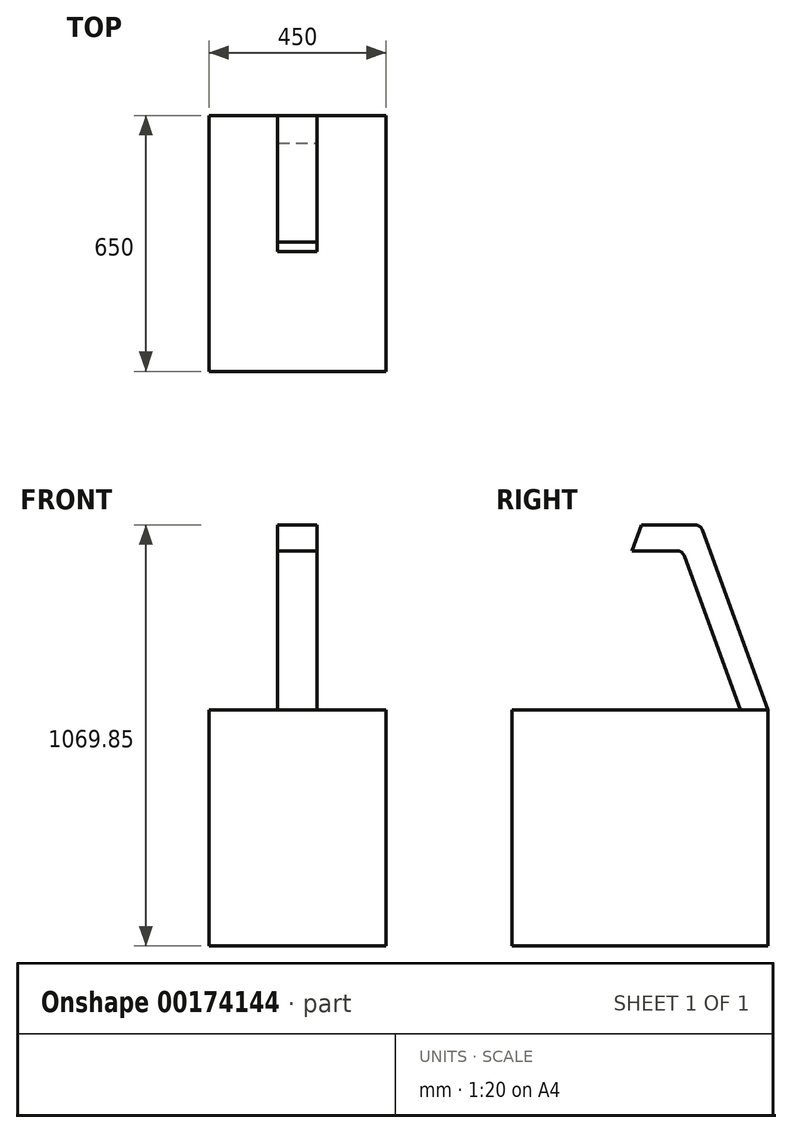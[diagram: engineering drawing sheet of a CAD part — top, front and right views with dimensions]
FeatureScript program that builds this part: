
annotation { "Feature Type Name" : "Feature", "Feature Type Description" : "" }
export const myFeature = defineFeature(function(context is Context, id is Id, definition is map)
    precondition{}
    {
        {
            var Q0;
            Q0=qCreatedBy(makeId("Top.planeOp"),FACE);
            var sketch = newSketch(context, id + "F0", { "sketchPlane" : qUnion([Q0])});
            skLineSegment(sketch, "E0.bottom", {"start": v(0, 0) * mm, "end": v(450, 0) * mm});
            skLineSegment(sketch, "E0.top", {"start": v(0, 650) * mm, "end": v(450, 650) * mm});
            skLineSegment(sketch, "E0.left", {"start": v(0, 0) * mm, "end": v(0, 650) * mm});
            skLineSegment(sketch, "E0.right", {"start": v(450, 0) * mm, "end": v(450, 650) * mm});
            skSolve(sketch);
        }
        {
            var Q0;
            Q0=makeQuery(id+"F0.imprint","IMPRINT",FACE,{"disambiguationData":[TD([[makeQuery(id+"F0.imprint","IMPRINT",EDGE,{"derivedFrom":sQuery(id+"F0.wireOp",EDGE,"E0.bottom")}),1.0]])]});
            extrude(context, id + "F1", {"entities" : qUnion([Q0]), "depth" : 600 * mm});
        }
        {
            var Q0;
            Q0=makeQuery(id+"F1.opExtrude","CAP_FACE",FACE,{"disambiguationData":[OSD([sQuery(id+"F0.wireOp",EDGE,"E0.bottom"),sQuery(id+"F0.wireOp",EDGE,"E0.top"),sQuery(id+"F0.wireOp",EDGE,"E0.left"),sQuery(id+"F0.wireOp",EDGE,"E0.right")])],"isStart":false});
            var sketch = newSketch(context, id + "F2", { "sketchPlane" : qUnion([Q0])});
            skLineSegment(sketch, "E1.bottom", {"start": v(175, 650) * mm, "end": v(275, 650) * mm});
            skLineSegment(sketch, "E1.top", {"start": v(175, 580) * mm, "end": v(275, 580) * mm});
            skLineSegment(sketch, "E1.left", {"start": v(175, 650) * mm, "end": v(175, 580) * mm});
            skLineSegment(sketch, "E1.right", {"start": v(275, 650) * mm, "end": v(275, 580) * mm});
            skSolve(sketch);
        }
        {
            var Q0;
            Q0=qCreatedBy(makeId("Right.planeOp"),FACE);
            var Q1;
            Q1=makeQuery(id+"F1.opExtrude","SWEPT_FACE",FACE,{"disambiguationData":[OSD([sQuery(id+"F0.wireOp",EDGE,"E0.right")])]});
            cPlane(context, id + "F3", {"entities" : qUnion([Q0, Q1]), "cplaneType" : CPlaneType.MID_PLANE, "offset" : 25 * mm, "width" : 150 * mm, "height" : 150 * mm});
        }
        {
            var Q0;
            Q0=qCreatedBy(id+"F3.planeOp",FACE);
            var sketch = newSketch(context, id + "F4", { "sketchPlane" : qUnion([Q0])});
            skLineSegment(sketch, "E2", {"start": v(650, 600) * mm, "end": v(478.99, 1069.85) * mm});
            skLineSegment(sketch, "E3", {"start": v(478.99, 1069.85) * mm, "end": v(328.99, 1069.85) * mm});
            skSolve(sketch);
        }
        {
            var Q0;
            Q0=makeQuery(id+"F2.imprint","IMPRINT",FACE,{"disambiguationData":[TD([[makeQuery(id+"F2.imprint","IMPRINT",EDGE,{"derivedFrom":sQuery(id+"F2.wireOp",EDGE,"E1.bottom")}),-1.0]])]});
            var Q1;
            Q1=qConstructionFilter(qBodyType(qCreatedBy(id+"F4",EDGE),BodyType.WIRE),ConstructionObject.NO);
            sweep(context, id + "F5", {"operationType" : NewBodyOperationType.ADD, "profiles" : qUnion([Q0]), "path" : qUnion([Q1])});
        }
        {
            var Q0;
            Q0=makeQuery(id+"F5.opSweep","MID_CAP_EDGE",EDGE,{"disambiguationData":[OSD([sQuery(id+"F2.wireOp",EDGE,"E1.bottom"),sQuery(id+"F4.wireOp",VERTEX,"E3.start")])],"capPos":1.0});
            var Q1;
            Q1=makeQuery(id+"F5.opSweep","MID_CAP_EDGE",EDGE,{"disambiguationData":[OSD([sQuery(id+"F2.wireOp",EDGE,"E1.top"),sQuery(id+"F4.wireOp",VERTEX,"E3.start")])],"capPos":1.0});
            fillet(context, id + "F6", {"entities" : qUnion([Q0, Q1]), "radius" : 20 * mm, "tangentPropagation" : true, "allowEdgeOverflow" : false});
        }
    });
